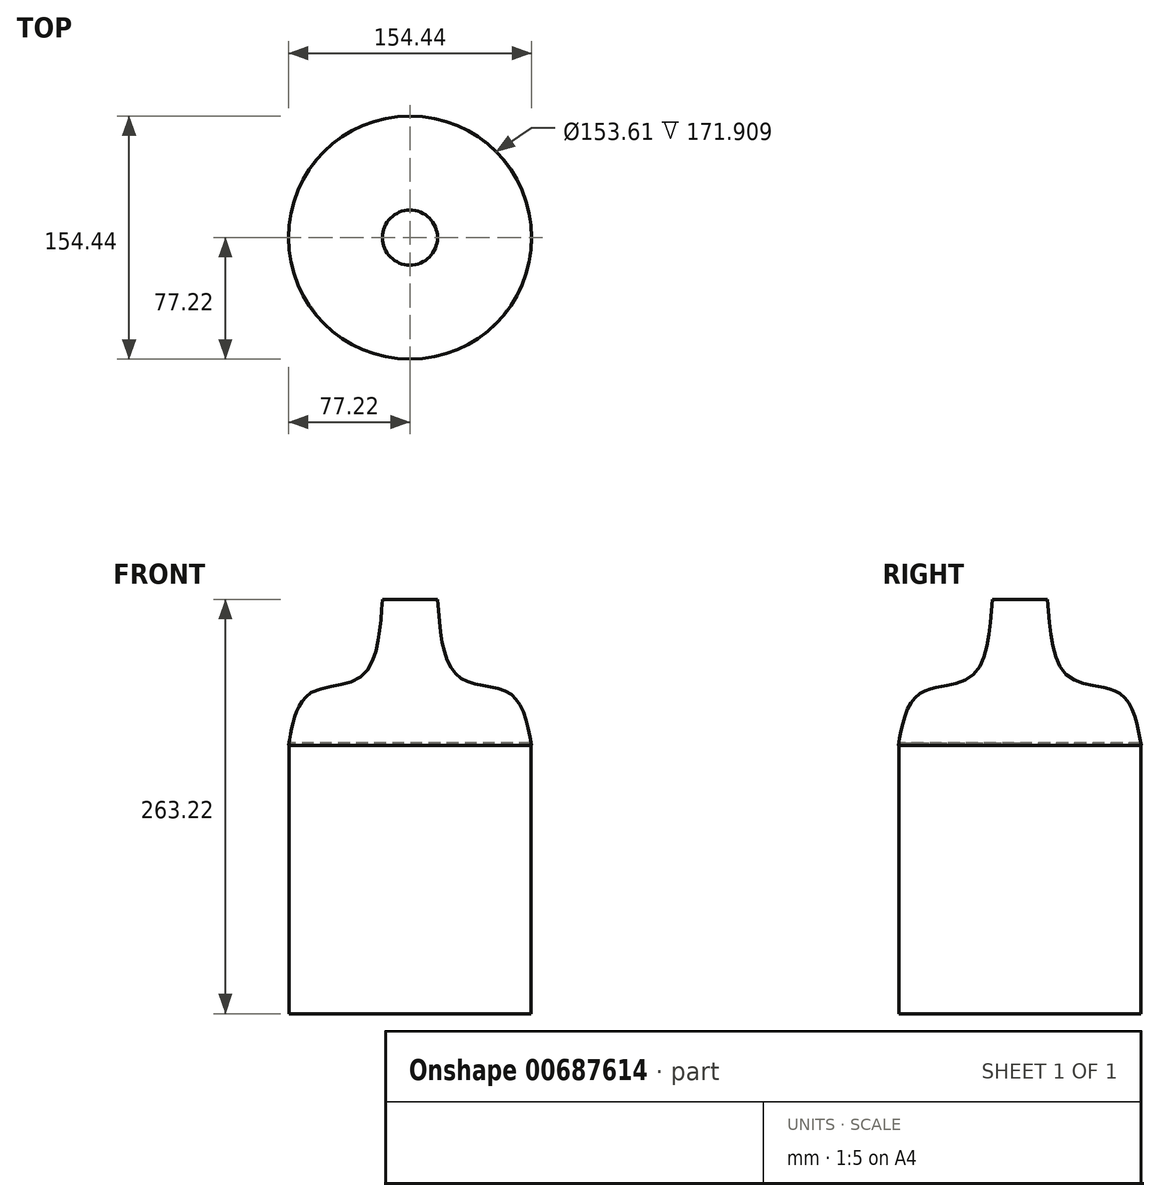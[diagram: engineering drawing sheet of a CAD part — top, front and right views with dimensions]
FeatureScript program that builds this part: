
annotation { "Feature Type Name" : "Feature", "Feature Type Description" : "" }
export const myFeature = defineFeature(function(context is Context, id is Id, definition is map)
    precondition{}
    {
        {
            var Q0;
            Q0=qCreatedBy(makeId("Front.planeOp"),FACE);
            var sketch = newSketch(context, id + "F0", { "sketchPlane" : qUnion([Q0])});
            skLineSegment(sketch, "E0", {"start": v(0, 0) * mm, "end": v(76.8, 0) * mm});
            skLineSegment(sketch, "E1", {"start": v(76.8, 0) * mm, "end": v(76.8, 171.9) * mm});
            skSolve(sketch);
        }
        {
            var Q0;
            Q0=qCreatedBy(makeId("Front.planeOp"),FACE);
            var sketch = newSketch(context, id + "F1", { "sketchPlane" : qUnion([Q0])});
            skLineSegment(sketch, "E2", {"start": v(0, 0) * mm, "end": v(0, 263.71) * mm});
            skLineSegment(sketch, "E3", {"start": v(0, 263.71) * mm, "end": v(17.55, 263.71) * mm});
            skSolve(sketch);
        }
        {
            var Q0;
            Q0=qCreatedBy(makeId("Front.planeOp"),FACE);
            var sketch = newSketch(context, id + "F2", { "sketchPlane" : qUnion([Q0])});
            skFitSpline(sketch, "E4", {"points": [v(77.22, 170.23) * mm, v(63.35, 203.47) * mm, v(31.16, 213.9) * mm, v(17.47, 263.22) * mm], "startDerivative": vector(-23.29, 130.03) * mm, "endDerivative": vector(-11.86, 164.16) * mm});
            skSolve(sketch);
        }
        {
            var Q0;
            Q0=sQuery(id+"F0.wireOp",EDGE,"E1");
            var Q1;
            Q1=sQuery(id+"F0.wireOp",EDGE,"E0");
            var Q2;
            Q2=sQuery(id+"F2.wireOp",EDGE,"E4");
            var Q3;
            Q3=sQuery(id+"F1.wireOp",EDGE,"E2");
            revolve(context, id + "F3", {"bodyType" : ToolBodyType.SURFACE, "surfaceEntities" : qUnion([Q0, Q1, Q2]), "axis" : qUnion([Q3]), "revolveType" : RevolveType.FULL});
        }
    });
